annotation { "Feature Type Name" : "Feature", "Feature Type Description" : "" }
export const myFeature = defineFeature(function(context is Context, id is Id, definition is map)
    precondition{}
    {
        {
            var Q0;
            Q0=qCreatedBy(makeId("Top.planeOp"),FACE);
            var sketch = newSketch(context, id + "F0", { "sketchPlane" : qUnion([Q0])});
            skLineSegment(sketch, "E0", {"start": v(0, 0) * mm, "end": v(0, 19.52) * mm});
            skLineSegment(sketch, "E1", {"start": v(-2.59, 22.02) * mm, "end": v(-15.71, 21.56) * mm});
            skLineSegment(sketch, "E2", {"start": v(-18.6, 18.46) * mm, "end": v(-18.6, 18.46) * mm});
            skLineSegment(sketch, "E3", {"start": v(-3, 19) * mm, "end": v(-3, 2) * mm});
            skLineSegment(sketch, "E4", {"start": v(-3, 2) * mm, "end": v(-17.6, 2.77) * mm});
            skLineSegment(sketch, "E5", {"start": v(-15.89, 0.68) * mm, "end": v(-3, 0) * mm});
            skLineSegment(sketch, "E6", {"start": v(0, 0) * mm, "end": v(0, -12.9) * mm});
            skLineSegment(sketch, "E7", {"start": v(-3, -12.9) * mm, "end": v(-3, 0) * mm});
            skArc(sketch, "E8", {"start": v(-18.6, 18.46) * mm, "mid": v(-18.09, 17.98) * mm, "end": v(-17.6, 18.5) * mm});
            skLineSegment(sketch, "E9.trimOffspring", {"start": v(-17.6, 18.5) * mm, "end": v(-3, 19) * mm});
            skArc(sketch, "E10", {"start": v(-17.6, 2.77) * mm, "mid": v(-18.08, 3.3) * mm, "end": v(-18.6, 2.82) * mm});
            skPoint(sketch, "E11.visualSharp", {"position": v(-18.7, 21.46) * mm});
            skArc(sketch, "E11.filletArc", {"start": v(-15.71, 21.56) * mm, "mid": v(-17.8, 20.6) * mm, "end": v(-18.6, 18.46) * mm});
            skPoint(sketch, "E12.visualSharp", {"position": v(-18.66, 0.82) * mm});
            skPoint(sketch, "E13.visualSharp", {"position": v(0, 22.1) * mm});
            skArc(sketch, "E13.filletArc", {"start": v(0, 19.52) * mm, "mid": v(-0.76, 21.32) * mm, "end": v(-2.59, 22.02) * mm});
            skArc(sketch, "E14", {"start": v(-3, -12.9) * mm, "mid": v(-1.5, -14.4) * mm, "end": v(0, -12.9) * mm});
            skArc(sketch, "E15", {"start": v(-18.6, 2.82) * mm, "mid": v(-17.59, 1.32) * mm, "end": v(-15.89, 0.68) * mm});
            skSolve(sketch);
        }
        {
            var Q0;
            Q0 = qSketchRegion(id + "F0", true);
            extrude(context, id + "F1", {"entities" : qUnion([Q0]), "depth" : 30 * mm, "offsetDistance" : 25 * mm});
        }
        {
            var Q0;
            Q0=makeQuery(id+"F1.opExtrude","SWEPT_FACE",FACE,{"disambiguationData":[OSD([sQuery(id+"F0.wireOp",EDGE,"E0"),sQuery(id+"F0.wireOp",EDGE,"E6")])]});
            var sketch = newSketch(context, id + "F2", { "sketchPlane" : qUnion([Q0])});
            skText(sketch, "E16", { "text": "Nein Lara", "fontName": "NotoSerif-BoldItalic.ttf"});
            const initialGuessF2  = {"E16": [-0.01059, 0.01873, 0.92362, -0.3833, 0.00416]};
            skSetInitialGuess(sketch, initialGuessF2);
            skSolve(sketch);
        }
        {
            var Q0;
            Q0 = qSketchRegion(id + "F2", true);
            var Q1;
            Q1 = qConstructionFilter(qBodyType(qCreatedBy(id + "F2" ,EDGE), BodyType.WIRE), ConstructionObject.NO);
            extrude(context, id + "F3", {"entities" : qUnion([Q0]), "operationType" : NewBodyOperationType.REMOVE, "surfaceEntities" : qUnion([Q1]), "oppositeDirection" : true, "depth" : 0.2 * mm, "offsetDistance" : 25 * mm});
        }
    });